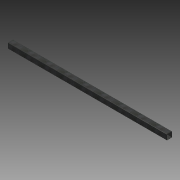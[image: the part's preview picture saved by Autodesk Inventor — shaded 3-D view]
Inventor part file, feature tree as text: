
AUTODESK INVENTOR PART (.ipt)
format: ipt  version: 2015 SP1 (Build 190203100, 203)  size: 88,064 bytes
history: native  units: in
note: dims shown in document units (in); Inventor stores cm internally (conversion verified against a paired STEP export)
features: extrude x1, fillet x1, sketch x1
ambient origin geometry x8: Origin, YZ Plane, XZ Plane, XY Plane, X Axis, Y Axis, Z Axis, Center Point
bodies: Solid1 (feature_tree)
feature tree (3):
  extrude  "Extrusion1"  Depth=2.0in
  fillet  "Fillet1"  Radius=0.083in
  sketch  "Sketch1"  dims[d0=2.0in d1=2.0in d2=0.083in d3=60.0in d4=0.0in d5=0.125in]
